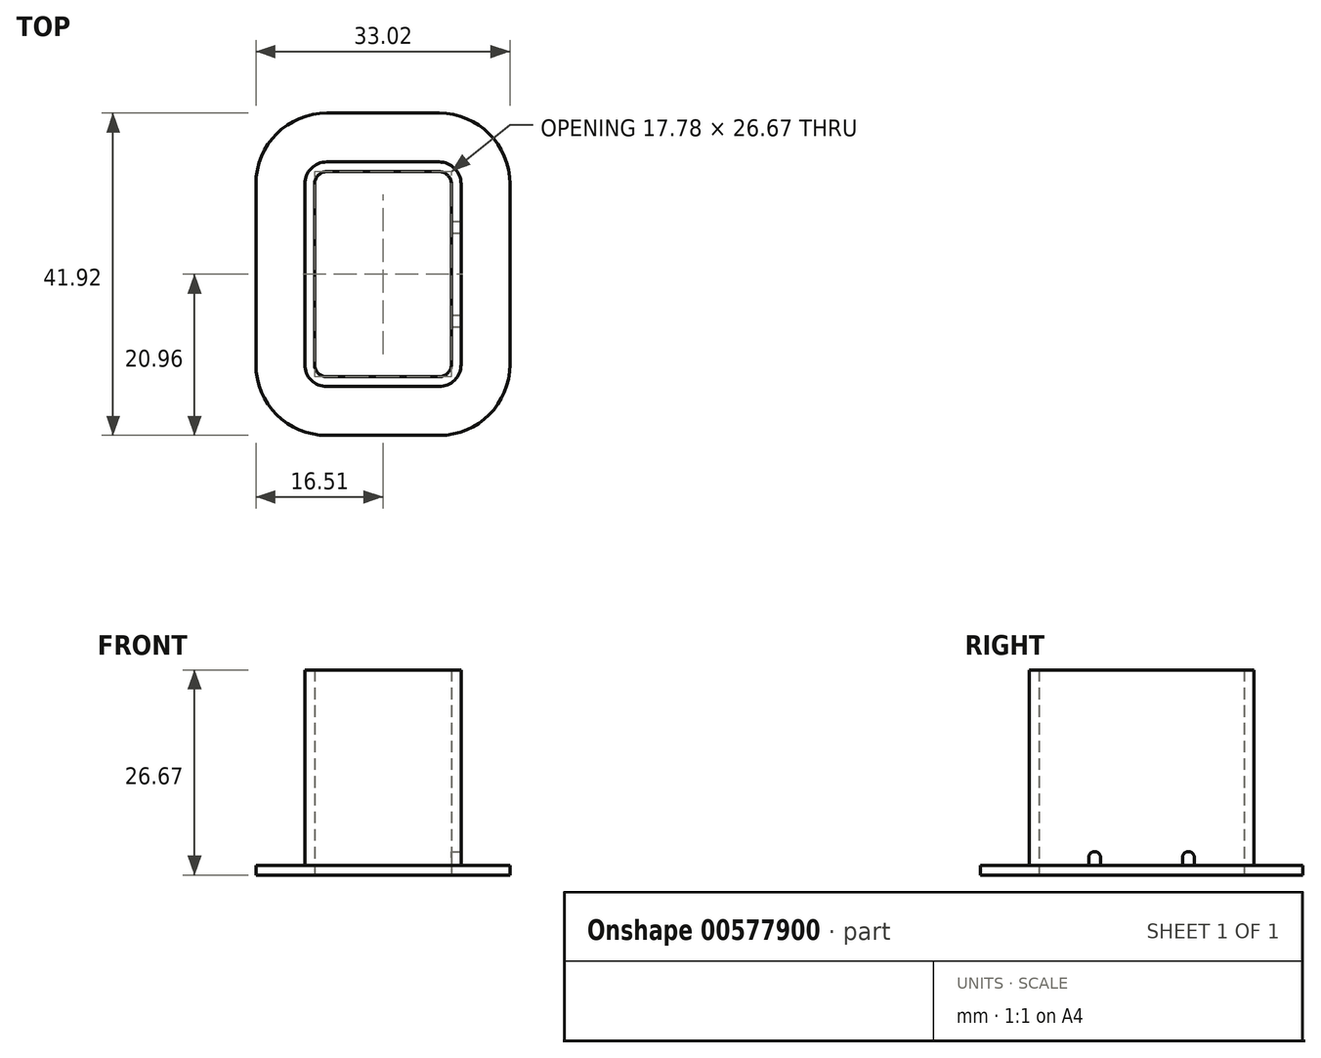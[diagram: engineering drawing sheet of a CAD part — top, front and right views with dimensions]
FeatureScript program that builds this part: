
annotation { "Feature Type Name" : "Feature", "Feature Type Description" : "" }
export const myFeature = defineFeature(function(context is Context, id is Id, definition is map)
    precondition{}
    {
        {
            var Q0;
            Q0=qCreatedBy(makeId("Top.planeOp"),FACE);
            var sketch = newSketch(context, id + "F0", { "sketchPlane" : qUnion([Q0])});
            skLineSegment(sketch, "E0.bottom", {"start": v(7.3, 13.34) * mm, "end": v(-7.3, 13.34) * mm});
            skLineSegment(sketch, "E0.top", {"start": v(7.3, -13.34) * mm, "end": v(-7.3, -13.34) * mm});
            skLineSegment(sketch, "E0.left", {"start": v(8.9, 11.75) * mm, "end": v(8.9, -11.75) * mm});
            skLineSegment(sketch, "E0.right", {"start": v(-8.9, 11.75) * mm, "end": v(-8.9, -11.75) * mm});
            skPoint(sketch, "E0.middle", {"position": v(0, 0) * mm});
            skPoint(sketch, "E1.visualSharp", {"position": v(-8.9, 13.34) * mm});
            skArc(sketch, "E1.filletArc", {"start": v(-7.3, 13.34) * mm, "mid": v(-8.43, 12.87) * mm, "end": v(-8.89, 11.75) * mm});
            skPoint(sketch, "E2.visualSharp", {"position": v(8.9, 13.34) * mm});
            skArc(sketch, "E2.filletArc", {"start": v(8.89, 11.75) * mm, "mid": v(8.43, 12.87) * mm, "end": v(7.3, 13.33) * mm});
            skPoint(sketch, "E3.visualSharp", {"position": v(8.9, -13.34) * mm});
            skArc(sketch, "E3.filletArc", {"start": v(7.3, -13.33) * mm, "mid": v(8.43, -12.87) * mm, "end": v(8.89, -11.75) * mm});
            skPoint(sketch, "E4.visualSharp", {"position": v(-8.9, -13.34) * mm});
            skArc(sketch, "E4.filletArc", {"start": v(-8.89, -11.75) * mm, "mid": v(-8.43, -12.87) * mm, "end": v(-7.3, -13.33) * mm});
            skArc(sketch, "E5.0", {"start": v(10.16, 11.75) * mm, "mid": v(9.32, 13.77) * mm, "end": v(7.3, 14.6) * mm});
            skLineSegment(sketch, "E5.1", {"start": v(10.16, 11.75) * mm, "end": v(10.16, -11.75) * mm});
            skLineSegment(sketch, "E5.2", {"start": v(7.3, 14.6) * mm, "end": v(-7.3, 14.6) * mm});
            skArc(sketch, "E5.3", {"start": v(7.3, -14.6) * mm, "mid": v(9.32, -13.77) * mm, "end": v(10.16, -11.75) * mm});
            skArc(sketch, "E5.4", {"start": v(-7.3, 14.6) * mm, "mid": v(-9.32, 13.77) * mm, "end": v(-10.16, 11.75) * mm});
            skLineSegment(sketch, "E5.5", {"start": v(-10.16, 11.75) * mm, "end": v(-10.16, -11.75) * mm});
            skArc(sketch, "E5.6", {"start": v(-10.16, -11.75) * mm, "mid": v(-9.32, -13.77) * mm, "end": v(-7.3, -14.6) * mm});
            skLineSegment(sketch, "E5.7", {"start": v(7.3, -14.6) * mm, "end": v(-7.3, -14.6) * mm});
            skArc(sketch, "E6.0", {"start": v(-7.3, 20.96) * mm, "mid": v(-13.81, 18.26) * mm, "end": v(-16.51, 11.75) * mm});
            skLineSegment(sketch, "E6.1", {"start": v(7.3, 20.96) * mm, "end": v(-7.3, 20.96) * mm});
            skLineSegment(sketch, "E6.2", {"start": v(-16.51, 11.75) * mm, "end": v(-16.51, -11.75) * mm});
            skArc(sketch, "E6.3", {"start": v(16.51, 11.75) * mm, "mid": v(13.81, 18.26) * mm, "end": v(7.3, 20.96) * mm});
            skArc(sketch, "E6.4", {"start": v(-16.51, -11.75) * mm, "mid": v(-13.81, -18.26) * mm, "end": v(-7.3, -20.96) * mm});
            skLineSegment(sketch, "E6.5", {"start": v(7.3, -20.96) * mm, "end": v(-7.3, -20.96) * mm});
            skArc(sketch, "E6.6", {"start": v(7.3, -20.96) * mm, "mid": v(13.81, -18.26) * mm, "end": v(16.51, -11.75) * mm});
            skLineSegment(sketch, "E6.7", {"start": v(16.51, 11.75) * mm, "end": v(16.51, -11.75) * mm});
            skSolve(sketch);
        }
        {
            var Q0;
            Q0=makeQuery(id+"F0.imprint","IMPRINT",FACE,{"disambiguationData":[TD([[makeQuery(id+"F0.imprint","IMPRINT",EDGE,{"derivedFrom":sQuery(id+"F0.wireOp",EDGE,"E0.bottom")}),-1.0]])]});
            extrude(context, id + "F1", {"entities" : qUnion([Q0]), "depth" : 25.4 * mm, "offsetDistance" : 25.4 * mm});
        }
        {
            var Q0;
            Q0 = qSketchRegion(id + "F0", true);
            var Q1;
            Q1=makeQuery(id+"F1.opExtrude","CAP_FACE",FACE,{"disambiguationData":[OSD([sQuery(id+"F0.wireOp",EDGE,"E0.bottom"),sQuery(id+"F0.wireOp",EDGE,"E0.top"),sQuery(id+"F0.wireOp",EDGE,"E0.left"),sQuery(id+"F0.wireOp",EDGE,"E0.right"),sQuery(id+"F0.wireOp",EDGE,"E1.filletArc"),sQuery(id+"F0.wireOp",EDGE,"E2.filletArc"),sQuery(id+"F0.wireOp",EDGE,"E3.filletArc"),sQuery(id+"F0.wireOp",EDGE,"E4.filletArc"),sQuery(id+"F0.wireOp",EDGE,"E5.0"),sQuery(id+"F0.wireOp",EDGE,"E5.1"),sQuery(id+"F0.wireOp",EDGE,"E5.2"),sQuery(id+"F0.wireOp",EDGE,"E5.3"),sQuery(id+"F0.wireOp",EDGE,"E5.4"),sQuery(id+"F0.wireOp",EDGE,"E5.5"),sQuery(id+"F0.wireOp",EDGE,"E5.6"),sQuery(id+"F0.wireOp",EDGE,"E5.7")])],"isStart":false});
            extrude(context, id + "F2", {"entities" : qUnion([Q0, Q1]), "operationType" : NewBodyOperationType.ADD, "depth" : 1.27 * mm, "offsetDistance" : 25.4 * mm});
        }
        {
            var Q0;
            {var subQ0=sQuery(id+"F0.wireOp",EDGE,"E5.1");Q0=makeQuery(id+"F2.boolean.opBoolean","MERGE",FACE,{"derivedFrom":[makeQuery(id+"F1.opExtrude","SWEPT_FACE",FACE,{"disambiguationData":[OSD([subQ0])]}),makeQuery(id+"F2.opExtrude","SWEPT_FACE",FACE,{"disambiguationData":[OSD([subQ0]),TDD([makeQuery(id+"F1.opExtrude","CAP_EDGE",EDGE,{"disambiguationData":[OSD([subQ0])],"isStart":false})])]})]});}
            var sketch = newSketch(context, id + "F3", { "sketchPlane" : qUnion([Q0])});
            skLineSegment(sketch, "E7", {"start": v(-6.86, 1.27) * mm, "end": v(-5.33, 1.27) * mm});
            skLineSegment(sketch, "E8", {"start": v(-5.33, 1.27) * mm, "end": v(-5.33, 2.29) * mm});
            skLineSegment(sketch, "E9", {"start": v(-6.86, 1.27) * mm, "end": v(-6.86, 2.29) * mm});
            skArc(sketch, "E10", {"start": v(-5.33, 2.29) * mm, "mid": v(-6.1, 3.05) * mm, "end": v(-6.86, 2.29) * mm});
            skArc(sketch, "E11.MirrorCS", {"start": v(5.33, 2.29) * mm, "mid": v(6.1, 3.05) * mm, "end": v(6.86, 2.29) * mm});
            skLineSegment(sketch, "E12.MirrorCS", {"start": v(5.33, 1.27) * mm, "end": v(5.33, 2.29) * mm});
            skLineSegment(sketch, "E13.MirrorCS", {"start": v(6.86, 1.27) * mm, "end": v(5.33, 1.27) * mm});
            skLineSegment(sketch, "E14.MirrorCS", {"start": v(6.86, 1.27) * mm, "end": v(6.86, 2.29) * mm});
            skSolve(sketch);
        }
        {
            var Q0;
            Q0 = qSketchRegion(id + "F3", true);
            extrude(context, id + "F4", {"entities" : qUnion([Q0]), "operationType" : NewBodyOperationType.REMOVE, "endBound" : BoundingType.UP_TO_NEXT, "oppositeDirection" : true, "depth" : 25.4 * mm, "offsetDistance" : 25.4 * mm});
        }
    });
